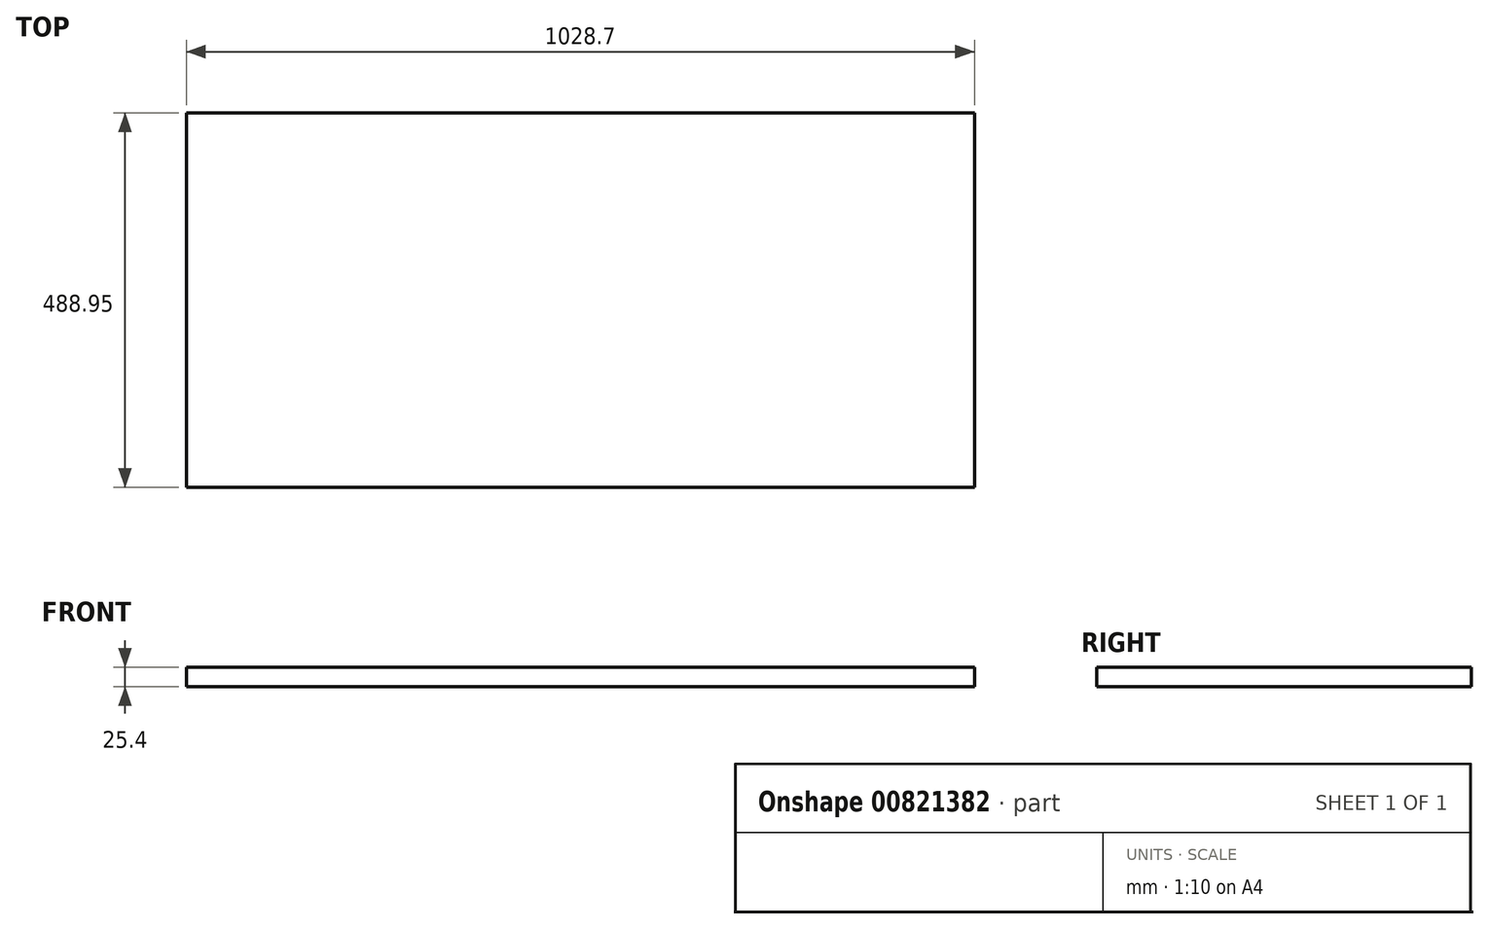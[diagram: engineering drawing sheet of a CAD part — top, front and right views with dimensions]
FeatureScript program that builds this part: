
annotation { "Feature Type Name" : "Feature", "Feature Type Description" : "" }
export const myFeature = defineFeature(function(context is Context, id is Id, definition is map)
    precondition{}
    {
        {
            var Q0;
            Q0=qCreatedBy(makeId("Top.planeOp"),FACE);
            var sketch = newSketch(context, id + "F0", { "sketchPlane" : qUnion([Q0])});
            skLineSegment(sketch, "E0.bottom", {"start": v(-534.56, -361.92) * mm, "end": v(494.14, -361.92) * mm});
            skLineSegment(sketch, "E0.top", {"start": v(-534.56, 127.03) * mm, "end": v(494.14, 127.03) * mm});
            skLineSegment(sketch, "E0.left", {"start": v(-534.56, -361.92) * mm, "end": v(-534.56, 127.03) * mm});
            skLineSegment(sketch, "E0.right", {"start": v(494.14, -361.92) * mm, "end": v(494.14, 127.03) * mm});
            skSolve(sketch);
        }
        {
            var Q0;
            Q0=makeQuery(id+"F0.imprint","IMPRINT",FACE,{"disambiguationData":[TD([[makeQuery(id+"F0.imprint","IMPRINT",EDGE,{"derivedFrom":sQuery(id+"F0.wireOp",EDGE,"E0.bottom")}),1.0]])]});
            extrude(context, id + "F1", {"entities" : qUnion([Q0]), "depth" : 25.4 * mm, "offsetDistance" : 25.4 * mm});
        }
    });
